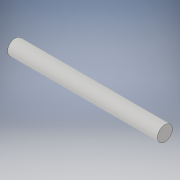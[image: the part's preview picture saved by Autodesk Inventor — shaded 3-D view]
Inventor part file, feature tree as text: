
AUTODESK INVENTOR PART (.ipt)
format: ipt  version: 2018 (Build 220112000, 112)  size: 93,184 bytes
history: native  units: in
note: dims shown in document units (in); Inventor stores cm internally (conversion verified against a paired STEP export)
features: sketch x2, revolve x1
ambient origin geometry x8: Origin, YZ Plane, XZ Plane, XY Plane, X Axis, Y Axis, Z Axis, Center Point
bodies: Solid1 (feature_tree)
feature tree (3):
  sketch  "Sketch1"  dims[d0=0.0689in d1=1.378in]
  revolve  "Revolution1"  [1 undecoded]
  sketch  "Sketch2"  dims[d2=90.0deg]
note: 1 required parameter value undecoded (feature->parameter linkage not recoverable at this tier; creation-order binding heuristic only, values carry confidence <= 0.55)
